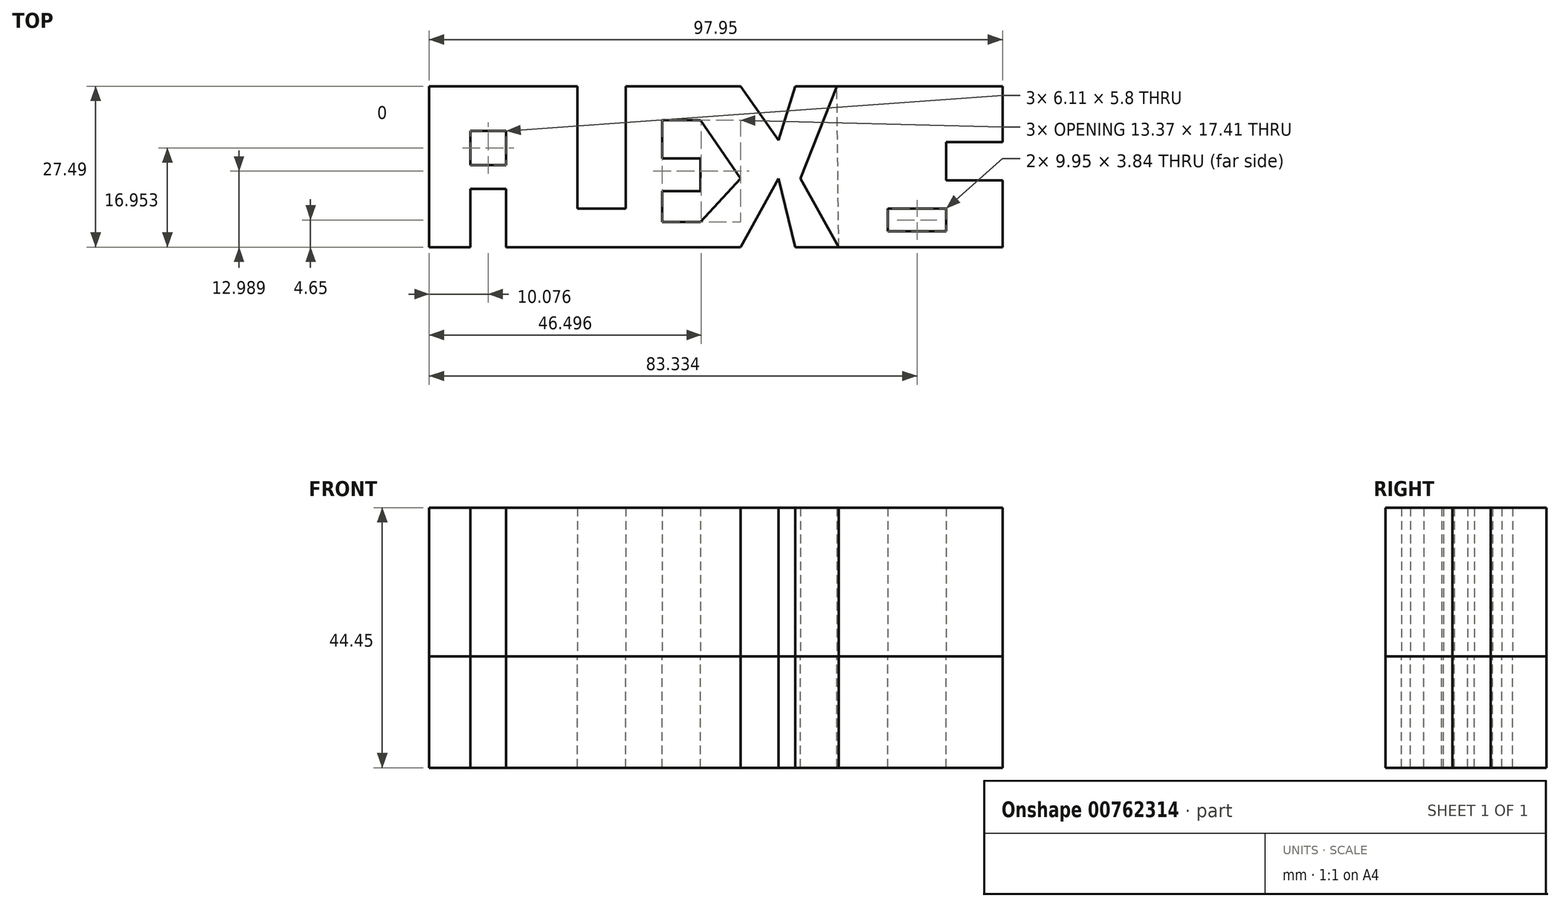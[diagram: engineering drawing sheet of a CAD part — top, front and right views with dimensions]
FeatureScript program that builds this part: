
annotation { "Feature Type Name" : "Feature", "Feature Type Description" : "" }
export const myFeature = defineFeature(function(context is Context, id is Id, definition is map)
    precondition{}
    {
        {
            var Q0;
            Q0=qCreatedBy(makeId("Top.planeOp"),FACE);
            var sketch = newSketch(context, id + "F0", { "sketchPlane" : qUnion([Q0])});
            skLineSegment(sketch, "E0", {"start": v(-59.7, -6.57) * mm, "end": v(-59.7, 20.92) * mm});
            skLineSegment(sketch, "E1", {"start": v(-59.7, 20.92) * mm, "end": v(-41.38, 20.92) * mm});
            skLineSegment(sketch, "E2", {"start": v(-59.7, -6.57) * mm, "end": v(-52.68, -6.57) * mm});
            skLineSegment(sketch, "E3", {"start": v(-52.68, -6.57) * mm, "end": v(-52.68, 3.36) * mm});
            skLineSegment(sketch, "E4", {"start": v(-52.68, 13.28) * mm, "end": v(-46.57, 13.28) * mm});
            skLineSegment(sketch, "E5", {"start": v(-46.57, 13.28) * mm, "end": v(-46.57, 7.48) * mm});
            skLineSegment(sketch, "E6", {"start": v(-46.57, -6.57) * mm, "end": v(-41.38, -6.57) * mm});
            skLineSegment(sketch, "E7", {"start": v(-41.38, -6.57) * mm, "end": v(-41.38, 20.92) * mm});
            skLineSegment(sketch, "E8", {"start": v(-52.68, 7.48) * mm, "end": v(-46.57, 7.48) * mm});
            skLineSegment(sketch, "E9", {"start": v(-46.57, 3.36) * mm, "end": v(-52.68, 3.36) * mm});
            skLineSegment(sketch, "E10.trimOffspring", {"start": v(-46.57, 3.36) * mm, "end": v(-46.57, -6.57) * mm});
            skLineSegment(sketch, "E11.trimOffspring", {"start": v(-52.68, 7.48) * mm, "end": v(-52.68, 13.28) * mm});
            skLineSegment(sketch, "E12", {"start": v(-41.38, 20.92) * mm, "end": v(-34.36, 20.92) * mm});
            skLineSegment(sketch, "E13", {"start": v(-34.36, 20.92) * mm, "end": v(-34.36, 0) * mm});
            skLineSegment(sketch, "E14", {"start": v(-34.36, 0) * mm, "end": v(-26.11, 0) * mm});
            skLineSegment(sketch, "E15", {"start": v(-26.11, -6.57) * mm, "end": v(-41.38, -6.57) * mm});
            skLineSegment(sketch, "E16", {"start": v(-26.11, 0) * mm, "end": v(-26.11, 20.92) * mm});
            skLineSegment(sketch, "E17", {"start": v(-26.11, 20.92) * mm, "end": v(-13.36, 20.92) * mm});
            skLineSegment(sketch, "E18", {"start": v(-13.36, 20.92) * mm, "end": v(-13.36, 15.12) * mm});
            skLineSegment(sketch, "E19", {"start": v(-13.36, 15.12) * mm, "end": v(-19.89, 15.12) * mm});
            skLineSegment(sketch, "E20", {"start": v(-19.89, 15.12) * mm, "end": v(-19.89, 8.6) * mm});
            skLineSegment(sketch, "E21", {"start": v(-19.89, 8.6) * mm, "end": v(-13.36, 8.6) * mm});
            skLineSegment(sketch, "E22", {"start": v(-13.36, 8.6) * mm, "end": v(-13.36, 3) * mm});
            skLineSegment(sketch, "E23", {"start": v(-13.36, 3) * mm, "end": v(-19.89, 3) * mm});
            skLineSegment(sketch, "E24", {"start": v(-19.89, 3) * mm, "end": v(-19.89, -2.28) * mm});
            skLineSegment(sketch, "E25", {"start": v(-13.36, -2.28) * mm, "end": v(-13.36, -6.57) * mm});
            skLineSegment(sketch, "E26", {"start": v(-13.36, -6.57) * mm, "end": v(-26.11, -6.57) * mm});
            skLineSegment(sketch, "E27", {"start": v(-13.36, -2.28) * mm, "end": v(-19.89, -2.28) * mm});
            skPoint(sketch, "E28", {"position": v(-41.38, 0) * mm});
            skLineSegment(sketch, "E29", {"start": v(-13.36, 20.92) * mm, "end": v(-6.52, 20.92) * mm});
            skLineSegment(sketch, "E30", {"start": v(-6.52, 20.92) * mm, "end": v(0, 11.7) * mm});
            skLineSegment(sketch, "E31", {"start": v(0, 11.7) * mm, "end": v(2.8, 20.92) * mm});
            skLineSegment(sketch, "E32", {"start": v(2.8, 20.92) * mm, "end": v(9.96, 20.92) * mm});
            skLineSegment(sketch, "E33", {"start": v(9.96, 20.92) * mm, "end": v(3.74, 5.18) * mm});
            skLineSegment(sketch, "E34", {"start": v(3.74, 5.18) * mm, "end": v(10.27, -6.57) * mm});
            skLineSegment(sketch, "E35", {"start": v(10.27, -6.57) * mm, "end": v(2.8, -6.57) * mm});
            skLineSegment(sketch, "E36", {"start": v(2.8, -6.57) * mm, "end": v(0, 5.18) * mm});
            skLineSegment(sketch, "E37", {"start": v(0, 5.18) * mm, "end": v(-6.52, -6.57) * mm});
            skLineSegment(sketch, "E38", {"start": v(-6.52, -6.57) * mm, "end": v(-13.36, -6.57) * mm});
            skLineSegment(sketch, "E39", {"start": v(-13.36, -2.28) * mm, "end": v(-6.52, 5.18) * mm});
            skLineSegment(sketch, "E40", {"start": v(-6.52, 5.18) * mm, "end": v(-13.36, 15.12) * mm});
            skLineSegment(sketch, "E41", {"start": v(10.27, -6.57) * mm, "end": v(9.96, 20.92) * mm});
            skLineSegment(sketch, "E42", {"start": v(18.66, -6.57) * mm, "end": v(10.27, -6.57) * mm});
            skLineSegment(sketch, "E43", {"start": v(9.96, 20.92) * mm, "end": v(18.66, 20.92) * mm});
            skLineSegment(sketch, "E44", {"start": v(38.25, 20.92) * mm, "end": v(18.66, 20.92) * mm});
            skLineSegment(sketch, "E45", {"start": v(38.25, 20.92) * mm, "end": v(38.25, 11.4) * mm});
            skLineSegment(sketch, "E46", {"start": v(38.25, 11.4) * mm, "end": v(28.6, 11.4) * mm});
            skLineSegment(sketch, "E47", {"start": v(28.6, 4.87) * mm, "end": v(28.6, 11.4) * mm});
            skLineSegment(sketch, "E48", {"start": v(28.6, 4.87) * mm, "end": v(38.25, 4.87) * mm});
            skLineSegment(sketch, "E49", {"start": v(38.25, 4.87) * mm, "end": v(38.25, -6.57) * mm});
            skLineSegment(sketch, "E50", {"start": v(38.25, -6.57) * mm, "end": v(18.66, -6.57) * mm});
            skLineSegment(sketch, "E51", {"start": v(18.66, 0) * mm, "end": v(28.6, 0) * mm});
            skLineSegment(sketch, "E52", {"start": v(28.6, 0) * mm, "end": v(28.6, -3.84) * mm});
            skLineSegment(sketch, "E53", {"start": v(28.6, -3.84) * mm, "end": v(18.66, -3.84) * mm});
            skLineSegment(sketch, "E54", {"start": v(18.66, 20.92) * mm, "end": v(18.66, -6.57) * mm});
            skLineSegment(sketch, "E55", {"start": v(-26.11, 0) * mm, "end": v(-26.11, -6.57) * mm});
            skSolve(sketch);
        }
        {
            var Q0;
            Q0=makeQuery(id+"F0.imprint","IMPRINT",FACE,{"disambiguationData":[TD([[makeQuery(id+"F0.imprint","IMPRINT",EDGE,{"derivedFrom":sQuery(id+"F0.wireOp",EDGE,"E0")}),-1.0]])]});
            var Q1;
            Q1=makeQuery(id+"F0.imprint","IMPRINT",FACE,{"disambiguationData":[TD([[makeQuery(id+"F0.imprint","IMPRINT",EDGE,{"derivedFrom":sQuery(id+"F0.wireOp",EDGE,"E16")}),-1.0]])]});
            var Q2;
            Q2=makeQuery(id+"F0.imprint","IMPRINT",FACE,{"disambiguationData":[TD([[makeQuery(id+"F0.imprint","IMPRINT",EDGE,{"derivedFrom":sQuery(id+"F0.wireOp",EDGE,"E41")}),-1.0]])]});
            var Q3;
            Q3=makeQuery(id+"F0.imprint","IMPRINT",FACE,{"disambiguationData":[TD([[makeQuery(id+"F0.imprint","IMPRINT",EDGE,{"derivedFrom":sQuery(id+"F0.wireOp",EDGE,"E7")}),-1.0]])]});
            var Q4;
            Q4=makeQuery(id+"F0.imprint","IMPRINT",FACE,{"disambiguationData":[TD([[makeQuery(id+"F0.imprint","IMPRINT",EDGE,{"derivedFrom":sQuery(id+"F0.wireOp",EDGE,"E18")}),1.0]])]});
            var Q5;
            {var subQ3=sQuery(id+"F0.wireOp",EDGE,"E44");Q5=makeQuery(id+"F0.imprint","IMPRINT",FACE,{"disambiguationData":[TD([[makeQuery(id+"F0.imprint","IMPRINT",EDGE,{"derivedFrom":subQ3}),1.0]])]});}
            extrude(context, id + "F1", {"entities" : qUnion([Q0, Q1, Q2, Q3, Q4, Q5]), "oppositeDirection" : true, "depth" : 19.05 * mm, "offsetDistance" : 25.4 * mm});
        }
        {
            var Q0;
            Q0=makeQuery(id+"F1.opExtrude","CAP_FACE",FACE,{"disambiguationData":[OSD([sQuery(id+"F0.wireOp",EDGE,"E0"),sQuery(id+"F0.wireOp",EDGE,"E1"),sQuery(id+"F0.wireOp",EDGE,"E2"),sQuery(id+"F0.wireOp",EDGE,"E3"),sQuery(id+"F0.wireOp",EDGE,"E4"),sQuery(id+"F0.wireOp",EDGE,"E5"),sQuery(id+"F0.wireOp",EDGE,"E6"),sQuery(id+"F0.wireOp",EDGE,"E8"),sQuery(id+"F0.wireOp",EDGE,"E9"),sQuery(id+"F0.wireOp",EDGE,"E10.trimOffspring"),sQuery(id+"F0.wireOp",EDGE,"E11.trimOffspring"),sQuery(id+"F0.wireOp",EDGE,"E12"),sQuery(id+"F0.wireOp",EDGE,"E13"),sQuery(id+"F0.wireOp",EDGE,"E14"),sQuery(id+"F0.wireOp",EDGE,"E15"),sQuery(id+"F0.wireOp",EDGE,"E16"),sQuery(id+"F0.wireOp",EDGE,"E17"),sQuery(id+"F0.wireOp",EDGE,"E19"),sQuery(id+"F0.wireOp",EDGE,"E20"),sQuery(id+"F0.wireOp",EDGE,"E21"),sQuery(id+"F0.wireOp",EDGE,"E22"),sQuery(id+"F0.wireOp",EDGE,"E23"),sQuery(id+"F0.wireOp",EDGE,"E24"),sQuery(id+"F0.wireOp",EDGE,"E26"),sQuery(id+"F0.wireOp",EDGE,"E27"),sQuery(id+"F0.wireOp",EDGE,"E29"),sQuery(id+"F0.wireOp",EDGE,"E30"),sQuery(id+"F0.wireOp",EDGE,"E31"),sQuery(id+"F0.wireOp",EDGE,"E32"),sQuery(id+"F0.wireOp",EDGE,"E33"),sQuery(id+"F0.wireOp",EDGE,"E34"),sQuery(id+"F0.wireOp",EDGE,"E35"),sQuery(id+"F0.wireOp",EDGE,"E36"),sQuery(id+"F0.wireOp",EDGE,"E37"),sQuery(id+"F0.wireOp",EDGE,"E38"),sQuery(id+"F0.wireOp",EDGE,"E39"),sQuery(id+"F0.wireOp",EDGE,"E40")])],"isStart":true});
            var Q1;
            Q1 = qSketchRegion(id + "F0", true);
            extrude(context, id + "F2", {"entities" : qUnion([Q0, Q1]), "depth" : 25.4 * mm, "offsetDistance" : 25.4 * mm});
        }
    });
